# Revit family: Heater_Wall_Electric_Bromic_SmartHeat_Eclipse_US
name_source: partatom
category: Specialty Equipment
units: mm (PartAtom-declared; Revit-internal decimal feet)

## family parameters
Cut with Voids When Loaded = No
Host = Face
OmniClass Number = 23.75.10.14
OmniClass Title = Independent Electric Heating Units
Part Type = Normal
Room Calculation Point = No
Round Connector Dimension = Use Diameter
Shared = No

## types (1)
- Standard
    Default Elevation = 87 "
    Depth_ANZRS = 61 "
    Description = Dim the lights and turn up the heat with our Eclipse Smart-Heat™ Electric heater. Available in six unique mounting options, the new Bromic Eclipse Smart-Heat™ series adds style, warmth and light to design-focused outdoor spaces.
    Diameter_ANZRS = 28 "
    FloorClearance = 96 "
    Frequency_ANZRS = 60 Hz
    Height_ANZRS = 22 "
    Manufacturer = Bromic Heating
    Material_ANZRS = Metal-Steel-Bromic-Black
    Model = Eclipse Smart-Heat™ Electric
    ModifiedIssue_ANZRS = 20210325.01 $
    PowerFactor_ANZRS = 1
    ProductCode_ANZRS = BH3230006
    SideClearance = 18 "
    URL = https://www.bromic.com
    Voltage_ANZRS = 240 V
    calcClearanceFront = 32 "
    calcClearanceWidth = 64 "

## geometry (parser evidence)
native form markers: Sweep x5
no freeform markers — native parametric forms only
